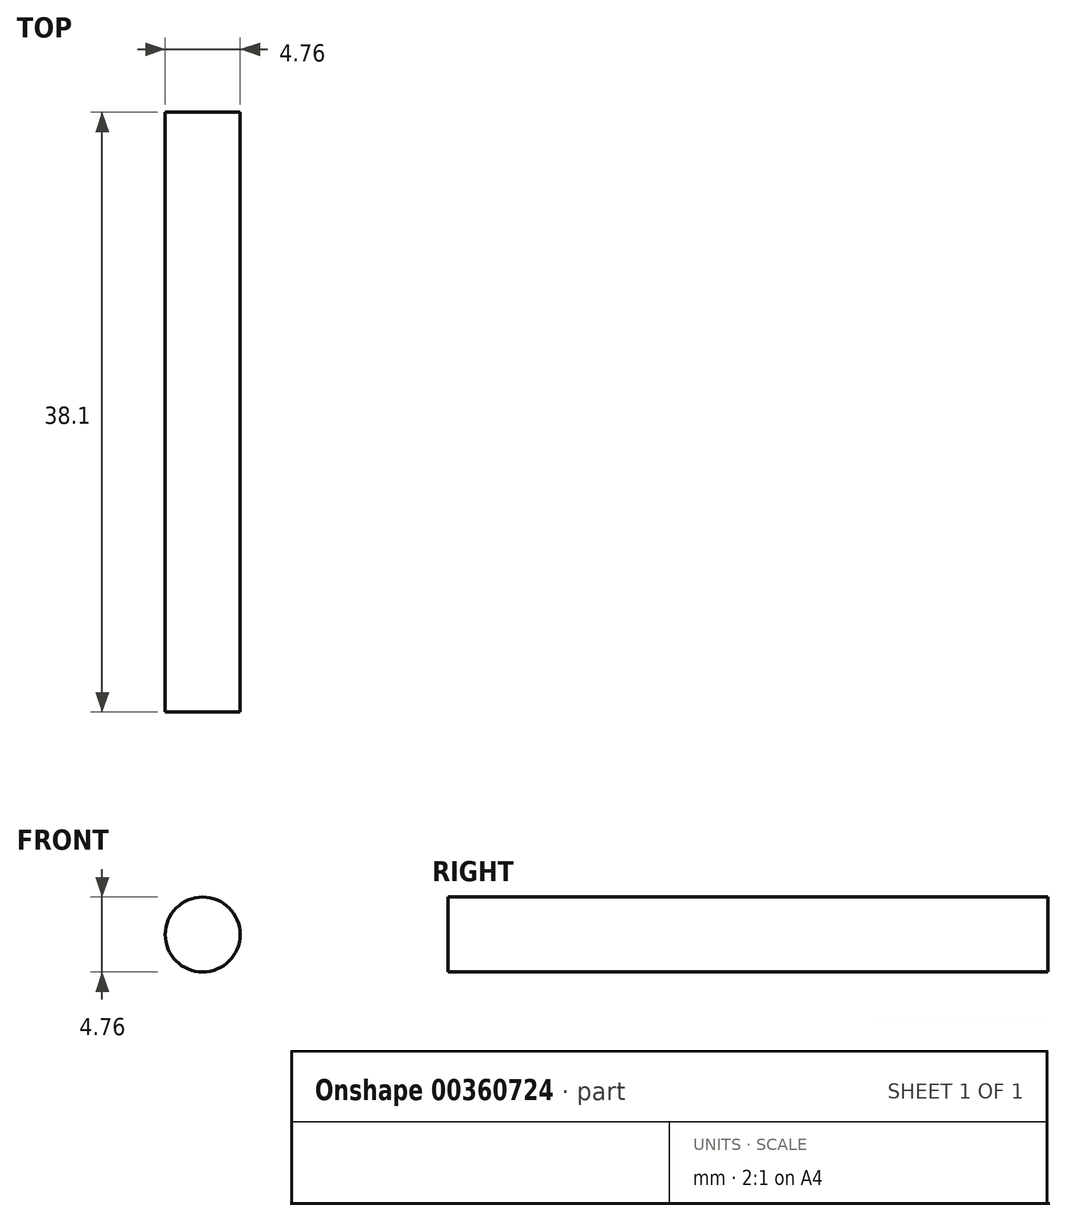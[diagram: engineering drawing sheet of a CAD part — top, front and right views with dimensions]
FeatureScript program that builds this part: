
annotation { "Feature Type Name" : "Feature", "Feature Type Description" : "" }
export const myFeature = defineFeature(function(context is Context, id is Id, definition is map)
    precondition{}
    {
        {
            var Q0;
            Q0=qCreatedBy(makeId("Front.planeOp"),FACE);
            var sketch = newSketch(context, id + "F0", { "sketchPlane" : qUnion([Q0])});
            skCircle(sketch, "E0", {"center": v(0, 0) * mm, "radius": 2.38 * mm});
            skSolve(sketch);
        }
        {
            var Q0;
            Q0=makeQuery(id+"F0.imprint","IMPRINT",FACE,{"disambiguationData":[TD([[makeQuery(id+"F0.imprint","IMPRINT",EDGE,{"derivedFrom":sQuery(id+"F0.wireOp",EDGE,"E0")}),1.0]])]});
            extrude(context, id + "F1", {"entities" : qUnion([Q0]), "depth" : 38.1 * mm, "symmetric" : true});
        }
    });
